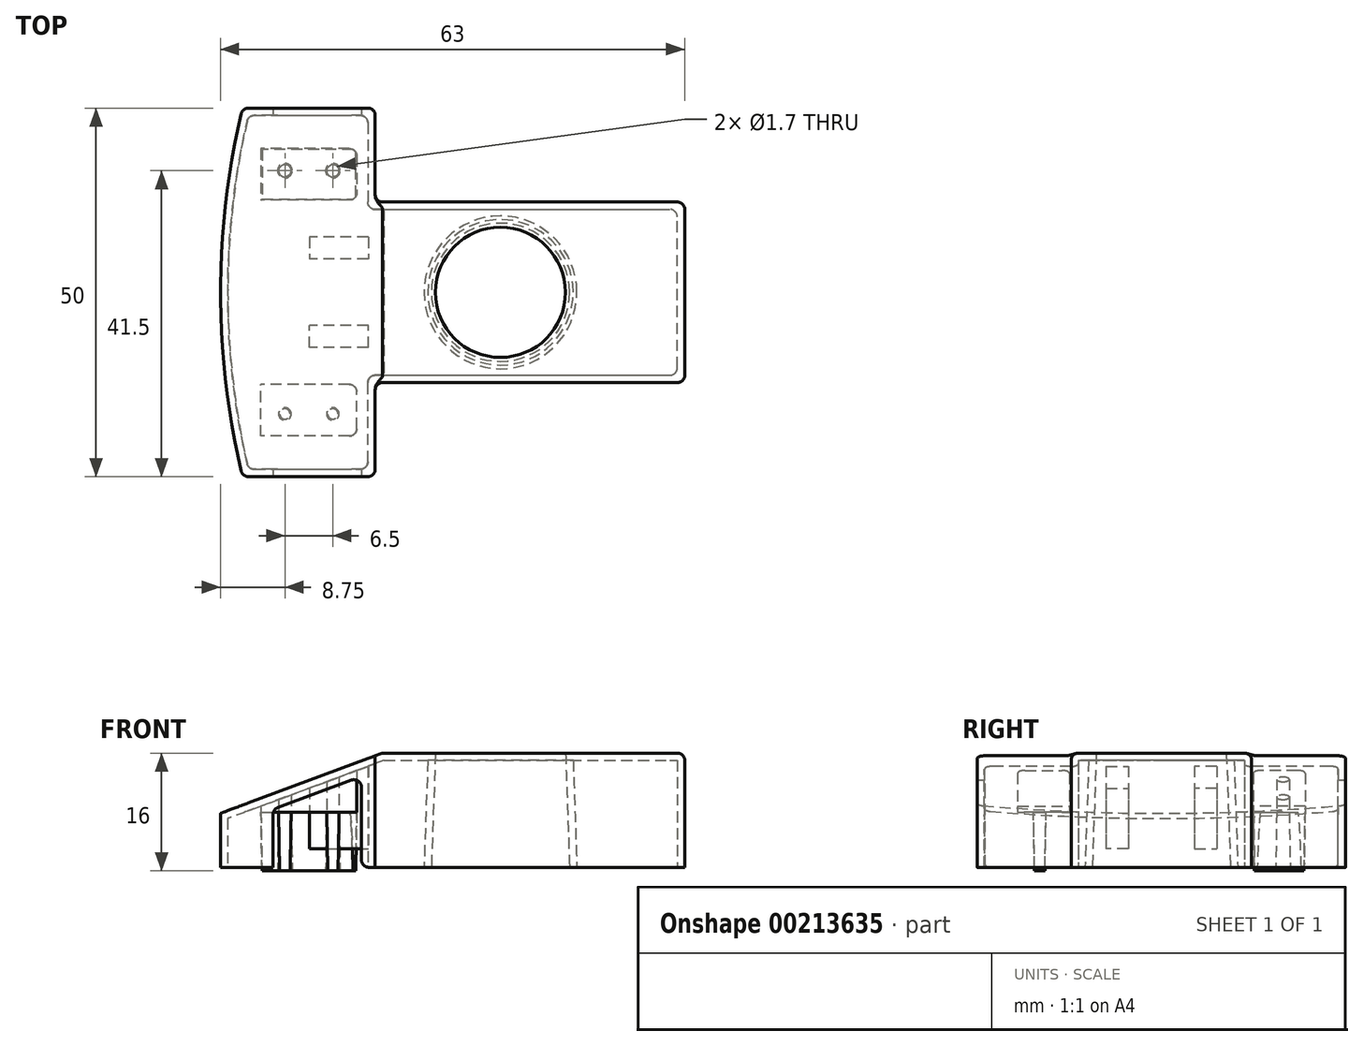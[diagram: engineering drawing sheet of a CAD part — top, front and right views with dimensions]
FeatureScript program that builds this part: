
annotation { "Feature Type Name" : "Feature", "Feature Type Description" : "" }
export const myFeature = defineFeature(function(context is Context, id is Id, definition is map)
    precondition{}
    {
        {
            var Q0;
            Q0=qCreatedBy(makeId("Top.planeOp"),FACE);
            var sketch = newSketch(context, id + "F0", { "sketchPlane" : qUnion([Q0])});
            skCircle(sketch, "E0", {"center": v(-4, 0) * mm, "radius": 9.37 * mm});
            skLineSegment(sketch, "E1.bottom", {"start": v(-21, -12.25) * mm, "end": v(21, -12.25) * mm});
            skLineSegment(sketch, "E1.top", {"start": v(-21, 12.25) * mm, "end": v(21, 12.25) * mm});
            skLineSegment(sketch, "E1.right", {"start": v(21, -12.25) * mm, "end": v(21, 12.25) * mm});
            skLineSegment(sketch, "E2.bottom", {"start": v(-21, -25) * mm, "end": v(-39, -25) * mm});
            skLineSegment(sketch, "E2.top", {"start": v(-21, 25) * mm, "end": v(-39, 25) * mm});
            skLineSegment(sketch, "E2.left", {"start": v(-21, -25) * mm, "end": v(-21, -12.25) * mm});
            skLineSegment(sketch, "E2.right", {"start": v(-39, -25) * mm, "end": v(-39, 25) * mm});
            skPoint(sketch, "E2.middle", {"position": v(-30, 0) * mm});
            skLineSegment(sketch, "E3.trimOffspring", {"start": v(-21, 12.25) * mm, "end": v(-21, 25) * mm});
            skLineSegment(sketch, "E4", {"start": v(-20, 12.25) * mm, "end": v(-20, -12.25) * mm});
            skPoint(sketch, "E5", {"position": v(-42, 0) * mm});
            skPoint(sketch, "E5.positionSnap0", {"position": v(-39, 0) * mm});
            skArc(sketch, "E6", {"start": v(-39, 25) * mm, "mid": v(-42, 0) * mm, "end": v(-39, -25) * mm});
            skSolve(sketch);
        }
        {
            var Q0;
            Q0=qSketchRegion(id+"F0",true);
            var Q1;
            Q1=makeQuery(id+"F0.imprint","IMPRINT",FACE,{"disambiguationData":[TD([[makeQuery(id+"F0.imprint","IMPRINT",EDGE,{"derivedFrom":sQuery(id+"F0.wireOp",EDGE,"E0")}),1.0]])]});
            extrude(context, id + "F1", {"entities" : qUnion([Q0, Q1]), "depth" : 15.5 * mm});
        }
        {
            var Q0;
            Q0=makeQuery(id+"F0.imprint","IMPRINT",FACE,{"disambiguationData":[TD([[makeQuery(id+"F0.imprint","IMPRINT",EDGE,{"derivedFrom":sQuery(id+"F0.wireOp",EDGE,"E0")}),1.0]])]});
            var Q1;
            Q1=makeQuery(id+"F1.opExtrude","CAP_FACE",FACE,{"disambiguationData":[OSD([sQuery(id+"F0.wireOp",EDGE,"E1.bottom"),sQuery(id+"F0.wireOp",EDGE,"E1.top"),sQuery(id+"F0.wireOp",EDGE,"E1.right"),sQuery(id+"F0.wireOp",EDGE,"E2.bottom"),sQuery(id+"F0.wireOp",EDGE,"E2.top"),sQuery(id+"F0.wireOp",EDGE,"E2.left"),sQuery(id+"F0.wireOp",EDGE,"E3.trimOffspring"),sQuery(id+"F0.wireOp",EDGE,"E6")])],"isStart":false});
            extrude(context, id + "F2", {"entities" : qUnion([Q0]), "operationType" : NewBodyOperationType.REMOVE, "endBound" : BoundingType.UP_TO_SURFACE, "endBoundEntityFace" : qUnion([Q1]), "depth" : 25 * mm, "hasDraft" : true, "draftAngle" : 2 * degree, "draftPullDirection" : true});
        }
        {
            var Q0;
            Q0=qCreatedBy(makeId("Front.planeOp"),FACE);
            var Q1;
            Q1=makeQuery(id+"F1.opExtrude","CAP_EDGE",EDGE,{"disambiguationData":[OSD([sQuery(id+"F0.wireOp",EDGE,"E2.bottom")])],"isStart":true});
            cPlane(context, id + "F3", {"entities" : qUnion([Q0, Q1]), "cplaneType" : CPlaneType.LINE_ANGLE, "offset" : 25 * mm, "angle" : 0 * degree, "width" : 150 * mm, "height" : 150 * mm});
        }
        {
            var Q0;
            Q0=qCreatedBy(id+"F3.planeOp",FACE);
            var sketch = newSketch(context, id + "F4", { "sketchPlane" : qUnion([Q0])});
            skLineSegment(sketch, "E7", {"start": v(20, 15.5) * mm, "end": v(42, 15.5) * mm});
            skLineSegment(sketch, "E8", {"start": v(42, 15.5) * mm, "end": v(42, 7.32) * mm});
            skLineSegment(sketch, "E9", {"start": v(42, 7.32) * mm, "end": v(20, 15.5) * mm});
            skLineSegment(sketch, "E10", {"start": v(42, 0) * mm, "end": v(41.46, 15.5) * mm, "construction": true});
            skLineSegment(sketch, "E11", {"start": v(42, 0) * mm, "end": v(42, 27.73) * mm, "construction": true});
            skSolve(sketch);
        }
        {
            var Q0;
            Q0=qSketchRegion(id+"F4",true);
            extrude(context, id + "F5", {"entities" : qUnion([Q0]), "operationType" : NewBodyOperationType.REMOVE, "endBound" : BoundingType.THROUGH_ALL, "depth" : 25 * mm});
        }
        {
            var Q0;
            Q0=makeQuery(id+"F1.opExtrude","CAP_FACE",FACE,{"disambiguationData":[OSD([sQuery(id+"F0.wireOp",EDGE,"E1.bottom"),sQuery(id+"F0.wireOp",EDGE,"E1.top"),sQuery(id+"F0.wireOp",EDGE,"E1.right"),sQuery(id+"F0.wireOp",EDGE,"E2.bottom"),sQuery(id+"F0.wireOp",EDGE,"E2.top"),sQuery(id+"F0.wireOp",EDGE,"E2.left"),sQuery(id+"F0.wireOp",EDGE,"E3.trimOffspring"),sQuery(id+"F0.wireOp",EDGE,"E6")])],"isStart":true});
            shell(context, id + "F6", {"entities" : qUnion([Q0]), "thickness" : 1 * mm});
        }
        {
            var Q0;
            Q0=makeQuery(id+"F1.opExtrude","SWEPT_FACE",FACE,{"disambiguationData":[OSD([sQuery(id+"F0.wireOp",EDGE,"E2.bottom")])]});
            var sketch = newSketch(context, id + "F7", { "sketchPlane" : qUnion([Q0])});
            skLineSegment(sketch, "E12", {"start": v(-20, 15.5) * mm, "end": v(-39, 8.43) * mm});
            skLineSegment(sketch, "E13", {"start": v(-39, 8.43) * mm, "end": v(-39, 15.5) * mm});
            skLineSegment(sketch, "E14", {"start": v(-39, 15.5) * mm, "end": v(-20, 15.5) * mm});
            skLineSegment(sketch, "E15", {"start": v(-34.87, 0) * mm, "end": v(-34.87, 7.86) * mm});
            skLineSegment(sketch, "E16", {"start": v(-34.87, 7.86) * mm, "end": v(-22.87, 12.32) * mm});
            skLineSegment(sketch, "E17", {"start": v(-22.87, 0) * mm, "end": v(-34.87, 0) * mm});
            skLineSegment(sketch, "E18", {"start": v(-22.87, 12.32) * mm, "end": v(-22.87, 0) * mm});
            skSolve(sketch);
        }
        {
            var Q0;
            Q0=makeQuery(id+"F7.imprint","IMPRINT",FACE,{"disambiguationData":[TD([[makeQuery(id+"F7.imprint","IMPRINT",EDGE,{"derivedFrom":sQuery(id+"F7.wireOp",EDGE,"E15")}),-1.0]])]});
            extrude(context, id + "F8", {"entities" : qUnion([Q0]), "operationType" : NewBodyOperationType.REMOVE, "endBound" : BoundingType.THROUGH_ALL, "oppositeDirection" : true, "depth" : 25 * mm});
        }
        {
            var Q0;
            Q0=makeQuery(id+"F1.opExtrude","CAP_FACE",FACE,{"disambiguationData":[OSD([sQuery(id+"F0.wireOp",EDGE,"E0"),sQuery(id+"F0.wireOp",EDGE,"E1.bottom"),sQuery(id+"F0.wireOp",EDGE,"E1.top"),sQuery(id+"F0.wireOp",EDGE,"E1.right"),sQuery(id+"F0.wireOp",EDGE,"E2.bottom"),sQuery(id+"F0.wireOp",EDGE,"E2.top"),sQuery(id+"F0.wireOp",EDGE,"E2.left"),sQuery(id+"F0.wireOp",EDGE,"E2.right"),sQuery(id+"F0.wireOp",EDGE,"E3.trimOffspring")])],"isStart":false});
            cPlane(context, id + "F9", {"entities" : qUnion([Q0]), "cplaneType" : CPlaneType.OFFSET, "offset" : 8 * mm, "oppositeDirection" : true, "width" : 150 * mm, "height" : 150 * mm});
        }
        {
            var Q0;
            Q0=qCreatedBy(id+"F9.planeOp",FACE);
            var sketch = newSketch(context, id + "F10", { "sketchPlane" : qUnion([Q0])});
            skLineSegment(sketch, "E19", {"start": v(0, 0) * mm, "end": v(-63, 0) * mm, "construction": true});
            skLineSegment(sketch, "E20.bottom", {"start": v(-36.5, -12.5) * mm, "end": v(-23.5, -12.5) * mm});
            skLineSegment(sketch, "E20.top", {"start": v(-36.5, -19.5) * mm, "end": v(-23.5, -19.5) * mm});
            skLineSegment(sketch, "E20.left", {"start": v(-36.5, -12.5) * mm, "end": v(-36.5, -19.5) * mm});
            skLineSegment(sketch, "E20.right", {"start": v(-23.5, -12.5) * mm, "end": v(-23.5, -19.5) * mm});
            skPoint(sketch, "E20.middle", {"position": v(-30, -16) * mm});
            skPoint(sketch, "E21", {"position": v(-33.25, -16.5) * mm});
            skPoint(sketch, "E22", {"position": v(-26.75, -16.5) * mm});
            skCircle(sketch, "E23", {"center": v(-33.25, -16.5) * mm, "radius": 0.85 * mm});
            skCircle(sketch, "E24", {"center": v(-26.75, -16.5) * mm, "radius": 0.85 * mm});
            skLineSegment(sketch, "E25.MirrorCS", {"start": v(-36.5, 12.5) * mm, "end": v(-23.5, 12.5) * mm});
            skLineSegment(sketch, "E26.MirrorCS", {"start": v(-36.5, 12.5) * mm, "end": v(-36.5, 19.5) * mm});
            skLineSegment(sketch, "E27.MirrorCS", {"start": v(-36.5, 19.5) * mm, "end": v(-23.5, 19.5) * mm});
            skLineSegment(sketch, "E28.MirrorCS", {"start": v(-23.5, 12.5) * mm, "end": v(-23.5, 19.5) * mm});
            skCircle(sketch, "E29.MirrorC", {"center": v(-26.75, 16.5) * mm, "radius": 0.85 * mm});
            skCircle(sketch, "E30.MirrorC", {"center": v(-33.25, 16.5) * mm, "radius": 0.85 * mm});
            skSolve(sketch);
        }
        {
            var Q0;
            Q0=makeQuery(id+"F10.imprint","IMPRINT",FACE,{"disambiguationData":[TD([[makeQuery(id+"F10.imprint","IMPRINT",EDGE,{"derivedFrom":sQuery(id+"F10.wireOp",EDGE,"E20.bottom")}),-1.0]])]});
            var Q1;
            Q1=makeQuery(id+"F10.imprint","IMPRINT",FACE,{"disambiguationData":[TD([[makeQuery(id+"F10.imprint","IMPRINT",EDGE,{"derivedFrom":sQuery(id+"F10.wireOp",EDGE,"E23")}),1.0]])]});
            var Q2;
            Q2=makeQuery(id+"F10.imprint","IMPRINT",FACE,{"disambiguationData":[TD([[makeQuery(id+"F10.imprint","IMPRINT",EDGE,{"derivedFrom":sQuery(id+"F10.wireOp",EDGE,"E24")}),1.0]])]});
            var Q3;
            Q3=makeQuery(id+"F10.imprint","IMPRINT",FACE,{"disambiguationData":[TD([[makeQuery(id+"F10.imprint","IMPRINT",EDGE,{"derivedFrom":sQuery(id+"F10.wireOp",EDGE,"E25.MirrorCS")}),1.0]])]});
            var Q4;
            Q4=makeQuery(id+"F10.imprint","IMPRINT",FACE,{"disambiguationData":[TD([[makeQuery(id+"F10.imprint","IMPRINT",EDGE,{"derivedFrom":sQuery(id+"F10.wireOp",EDGE,"E30.MirrorC")}),-1.0]])]});
            var Q5;
            Q5=makeQuery(id+"F10.imprint","IMPRINT",FACE,{"disambiguationData":[TD([[makeQuery(id+"F10.imprint","IMPRINT",EDGE,{"derivedFrom":sQuery(id+"F10.wireOp",EDGE,"E29.MirrorC")}),-1.0]])]});
            var Q6;
            Q6=makeQuery(id+"F6.opShell","OFFSET_FACE",FACE,{"disambiguationData":[OSD([sQuery(id+"F4.wireOp",EDGE,"E9")])]});
            extrude(context, id + "F11", {"entities" : qUnion([Q0, Q1, Q2, Q3, Q4, Q5]), "operationType" : NewBodyOperationType.ADD, "endBound" : BoundingType.UP_TO_SURFACE, "endBoundEntityFace" : qUnion([Q6]), "depth" : 25 * mm});
        }
        {
            var Q0;
            Q0=makeQuery(id+"F10.imprint","IMPRINT",FACE,{"disambiguationData":[TD([[makeQuery(id+"F10.imprint","IMPRINT",EDGE,{"derivedFrom":sQuery(id+"F10.wireOp",EDGE,"E23")}),1.0]])]});
            var Q1;
            Q1=makeQuery(id+"F10.imprint","IMPRINT",FACE,{"disambiguationData":[TD([[makeQuery(id+"F10.imprint","IMPRINT",EDGE,{"derivedFrom":sQuery(id+"F10.wireOp",EDGE,"E29.MirrorC")}),-1.0]])]});
            var Q2;
            Q2=makeQuery(id+"F10.imprint","IMPRINT",FACE,{"disambiguationData":[TD([[makeQuery(id+"F10.imprint","IMPRINT",EDGE,{"derivedFrom":sQuery(id+"F10.wireOp",EDGE,"E30.MirrorC")}),-1.0]])]});
            var Q3;
            Q3=makeQuery(id+"F10.imprint","IMPRINT",FACE,{"disambiguationData":[TD([[makeQuery(id+"F10.imprint","IMPRINT",EDGE,{"derivedFrom":sQuery(id+"F10.wireOp",EDGE,"E24")}),1.0]])]});
            extrude(context, id + "F12", {"entities" : qUnion([Q0, Q1, Q2, Q3]), "operationType" : NewBodyOperationType.ADD, "oppositeDirection" : true, "depth" : 8 * mm, "hasDraft" : true, "draftAngle" : 1 * degree, "draftPullDirection" : true});
        }
        {
            var Q0;
            Q0=makeQuery(id+"F1.opExtrude","CAP_EDGE",EDGE,{"disambiguationData":[OSD([sQuery(id+"F0.wireOp",EDGE,"E1.bottom")])],"isStart":false});
            var Q1;
            Q1=makeQuery(id+"F1.opExtrude","CAP_EDGE",EDGE,{"disambiguationData":[OSD([sQuery(id+"F0.wireOp",EDGE,"E1.right")])],"isStart":false});
            var Q2;
            Q2=makeQuery(id+"F1.opExtrude","CAP_EDGE",EDGE,{"disambiguationData":[OSD([sQuery(id+"F0.wireOp",EDGE,"E1.top")])],"isStart":false});
            var Q3;
            Q3=makeQuery(id+"F1.opExtrude","SWEPT_EDGE",EDGE,{"disambiguationData":[OSD([sQuery(id+"F0.wireOp",EDGE,"E1.bottom"),sQuery(id+"F0.wireOp",EDGE,"E1.right")])]});
            var Q4;
            Q4=makeQuery(id+"F1.opExtrude","SWEPT_EDGE",EDGE,{"disambiguationData":[OSD([sQuery(id+"F0.wireOp",EDGE,"E1.top"),sQuery(id+"F0.wireOp",EDGE,"E1.right")])]});
            fillet(context, id + "F13", {"entities" : qUnion([Q0, Q1, Q2, Q3, Q4]), "radius" : 1 * mm, "tangentPropagation" : true, "allowEdgeOverflow" : false});
        }
        {
            var Q0;
            Q0=makeQuery(id+"F1.opExtrude","SWEPT_EDGE",EDGE,{"disambiguationData":[OSD([sQuery(id+"F0.wireOp",EDGE,"E2.bottom"),sQuery(id+"F0.wireOp",EDGE,"E2.left")])]});
            var Q1;
            Q1=makeQuery(id+"F5.boolean.opBoolean","INTERSECT",EDGE,{"derivedFrom":[makeQuery(id+"F1.opExtrude","SWEPT_FACE",FACE,{"disambiguationData":[OSD([sQuery(id+"F0.wireOp",EDGE,"E2.left")])]}),makeQuery(id+"F5.opExtrude","SWEPT_FACE",FACE,{"disambiguationData":[OSD([sQuery(id+"FjstzwEYRuGCUyq_1.wireOp",EDGE,"6156deb2-2619-4c56-9df6-34b3699534c4")])]})]});
            var Q2;
            Q2=makeQuery(id+"F5.boolean.opBoolean","COPY",EDGE,{"derivedFrom":makeQuery(id+"F5.opExtrude","CAP_EDGE",EDGE,{"disambiguationData":[OSD([sQuery(id+"FjstzwEYRuGCUyq_1.wireOp",EDGE,"6156deb2-2619-4c56-9df6-34b3699534c4")])],"isStart":true})});
            var Q3;
            Q3=makeQuery(id+"F1.opExtrude","SWEPT_EDGE",EDGE,{"disambiguationData":[OSD([sQuery(id+"F0.wireOp",EDGE,"E2.bottom"),sQuery(id+"F0.wireOp",EDGE,"E2.right"),sQuery(id+"F0.wireOp",EDGE,"E6")])]});
            var Q4;
            Q4=makeQuery(id+"F5.boolean.opBoolean","INTERSECT",EDGE,{"derivedFrom":[makeQuery(id+"F1.opExtrude","SWEPT_FACE",FACE,{"disambiguationData":[OSD([sQuery(id+"F0.wireOp",EDGE,"E6")])]}),makeQuery(id+"F5.opExtrude","SWEPT_FACE",FACE,{"disambiguationData":[OSD([sQuery(id+"FjstzwEYRuGCUyq_1.wireOp",EDGE,"6156deb2-2619-4c56-9df6-34b3699534c4")])]})]});
            var Q5;
            Q5=makeQuery(id+"F5.boolean.opBoolean","INTERSECT",EDGE,{"derivedFrom":[makeQuery(id+"F1.opExtrude","SWEPT_FACE",FACE,{"disambiguationData":[OSD([sQuery(id+"F0.wireOp",EDGE,"E2.top")])]}),makeQuery(id+"F5.opExtrude","SWEPT_FACE",FACE,{"disambiguationData":[OSD([sQuery(id+"FjstzwEYRuGCUyq_1.wireOp",EDGE,"6156deb2-2619-4c56-9df6-34b3699534c4")])]})]});
            var Q6;
            Q6=makeQuery(id+"F1.opExtrude","SWEPT_EDGE",EDGE,{"disambiguationData":[OSD([sQuery(id+"F0.wireOp",EDGE,"E2.top"),sQuery(id+"F0.wireOp",EDGE,"E2.right"),sQuery(id+"F0.wireOp",EDGE,"E6")])]});
            var Q7;
            Q7=makeQuery(id+"F1.opExtrude","SWEPT_EDGE",EDGE,{"disambiguationData":[OSD([sQuery(id+"F0.wireOp",EDGE,"E2.top"),sQuery(id+"F0.wireOp",EDGE,"E3.trimOffspring")])]});
            var Q8;
            Q8=makeQuery(id+"F5.boolean.opBoolean","INTERSECT",EDGE,{"derivedFrom":[makeQuery(id+"F1.opExtrude","SWEPT_FACE",FACE,{"disambiguationData":[OSD([sQuery(id+"F0.wireOp",EDGE,"E3.trimOffspring")])]}),makeQuery(id+"F5.opExtrude","SWEPT_FACE",FACE,{"disambiguationData":[OSD([sQuery(id+"FjstzwEYRuGCUyq_1.wireOp",EDGE,"6156deb2-2619-4c56-9df6-34b3699534c4")])]})]});
            fillet(context, id + "F14", {"entities" : qUnion([Q0, Q1, Q2, Q3, Q4, Q5, Q6, Q7, Q8]), "radius" : 1 * mm, "tangentPropagation" : true, "allowEdgeOverflow" : false});
        }
        {
            var Q0;
            Q0=makeQuery(id+"F1.opExtrude","SWEPT_EDGE",EDGE,{"disambiguationData":[OSD([sQuery(id+"F0.wireOp",EDGE,"E1.top"),sQuery(id+"F0.wireOp",EDGE,"E3.trimOffspring")])]});
            fillet(context, id + "F15", {"entities" : qUnion([Q0]), "radius" : 1 * mm, "tangentPropagation" : true, "allowEdgeOverflow" : false});
        }
        {
            var Q0;
            Q0=makeQuery(id+"F1.opExtrude","SWEPT_EDGE",EDGE,{"disambiguationData":[OSD([sQuery(id+"F0.wireOp",EDGE,"E1.bottom"),sQuery(id+"F0.wireOp",EDGE,"E2.left")])]});
            var Q1;
            {var subQ0=sQuery(id+"F0.wireOp",EDGE,"E2.bottom");var subQ1=sQuery(id+"F7.wireOp",EDGE,"E18");Q1=makeQuery(id+"F8.boolean.opBoolean","COPY",EDGE,{"disambiguationData":[TD([makeQuery(id+"F1.opExtrude","SWEPT_FACE",FACE,{"disambiguationData":[OSD([subQ0])]})])],"derivedFrom":makeQuery(id+"F8.opExtrude","SWEPT_EDGE",EDGE,{"disambiguationData":[OSD([subQ0,sQuery(id+"F7.wireOp",EDGE,"E17"),subQ1])]})});}
            var Q2;
            {var subQ0=sQuery(id+"F0.wireOp",EDGE,"E2.bottom");var subQ1=sQuery(id+"F7.wireOp",EDGE,"E15");Q2=makeQuery(id+"F8.boolean.opBoolean","COPY",EDGE,{"disambiguationData":[TD([makeQuery(id+"F1.opExtrude","SWEPT_FACE",FACE,{"disambiguationData":[OSD([subQ0])]})])],"derivedFrom":makeQuery(id+"F8.opExtrude","SWEPT_EDGE",EDGE,{"disambiguationData":[OSD([subQ0,subQ1,sQuery(id+"F7.wireOp",EDGE,"E17")])]})});}
            var Q3;
            {var subQ0=sQuery(id+"F0.wireOp",EDGE,"E2.top");var subQ1=sQuery(id+"F0.wireOp",EDGE,"E2.bottom");var subQ2=sQuery(id+"F7.wireOp",EDGE,"E15");Q3=makeQuery(id+"F8.boolean.opBoolean","COPY",EDGE,{"disambiguationData":[TD([makeQuery(id+"F1.opExtrude","SWEPT_FACE",FACE,{"disambiguationData":[OSD([subQ0])]})])],"derivedFrom":makeQuery(id+"F8.opExtrude","SWEPT_EDGE",EDGE,{"disambiguationData":[OSD([subQ1,subQ2,sQuery(id+"F7.wireOp",EDGE,"E17")])]})});}
            var Q4;
            {var subQ0=sQuery(id+"F0.wireOp",EDGE,"E2.top");var subQ1=sQuery(id+"F0.wireOp",EDGE,"E2.bottom");var subQ2=sQuery(id+"F7.wireOp",EDGE,"E18");Q4=makeQuery(id+"F8.boolean.opBoolean","COPY",EDGE,{"disambiguationData":[TD([makeQuery(id+"F1.opExtrude","SWEPT_FACE",FACE,{"disambiguationData":[OSD([subQ0])]})])],"derivedFrom":makeQuery(id+"F8.opExtrude","SWEPT_EDGE",EDGE,{"disambiguationData":[OSD([subQ1,sQuery(id+"F7.wireOp",EDGE,"E17"),subQ2])]})});}
            var Q5;
            {var subQ0=sQuery(id+"F0.wireOp",EDGE,"E2.top");var subQ1=sQuery(id+"F7.wireOp",EDGE,"E18");var subQ2=sQuery(id+"F7.wireOp",EDGE,"E16");Q5=makeQuery(id+"F8.boolean.opBoolean","COPY",EDGE,{"disambiguationData":[TD([makeQuery(id+"F1.opExtrude","SWEPT_FACE",FACE,{"disambiguationData":[OSD([subQ0])]})])],"derivedFrom":makeQuery(id+"F8.opExtrude","SWEPT_EDGE",EDGE,{"disambiguationData":[OSD([subQ2,subQ1])]})});}
            var Q6;
            {var subQ0=sQuery(id+"F0.wireOp",EDGE,"E2.top");var subQ1=sQuery(id+"F7.wireOp",EDGE,"E15");var subQ2=sQuery(id+"F7.wireOp",EDGE,"E16");Q6=makeQuery(id+"F8.boolean.opBoolean","COPY",EDGE,{"disambiguationData":[TD([makeQuery(id+"F1.opExtrude","SWEPT_FACE",FACE,{"disambiguationData":[OSD([subQ0])]})])],"derivedFrom":makeQuery(id+"F8.opExtrude","SWEPT_EDGE",EDGE,{"disambiguationData":[OSD([subQ1,subQ2])]})});}
            var Q7;
            {var subQ0=sQuery(id+"F0.wireOp",EDGE,"E2.bottom");var subQ1=sQuery(id+"F7.wireOp",EDGE,"E18");var subQ2=sQuery(id+"F7.wireOp",EDGE,"E16");Q7=makeQuery(id+"F8.boolean.opBoolean","COPY",EDGE,{"disambiguationData":[TD([makeQuery(id+"F1.opExtrude","SWEPT_FACE",FACE,{"disambiguationData":[OSD([subQ0])]})])],"derivedFrom":makeQuery(id+"F8.opExtrude","SWEPT_EDGE",EDGE,{"disambiguationData":[OSD([subQ2,subQ1])]})});}
            var Q8;
            {var subQ0=sQuery(id+"F0.wireOp",EDGE,"E2.bottom");var subQ1=sQuery(id+"F7.wireOp",EDGE,"E15");var subQ2=sQuery(id+"F7.wireOp",EDGE,"E16");Q8=makeQuery(id+"F8.boolean.opBoolean","COPY",EDGE,{"disambiguationData":[TD([makeQuery(id+"F1.opExtrude","SWEPT_FACE",FACE,{"disambiguationData":[OSD([subQ0])]})])],"derivedFrom":makeQuery(id+"F8.opExtrude","SWEPT_EDGE",EDGE,{"disambiguationData":[OSD([subQ1,subQ2])]})});}
            var Q9;
            Q9=makeQuery(id+"F6.opShell","OFFSET_EDGE",EDGE,{"disambiguationData":[OSD([sQuery(id+"F0.wireOp",EDGE,"E1.top"),sQuery(id+"F0.wireOp",EDGE,"E3.trimOffspring")])]});
            var Q10;
            Q10=makeQuery(id+"F6.opShell","OFFSET_EDGE",EDGE,{"disambiguationData":[OSD([sQuery(id+"F0.wireOp",EDGE,"E1.bottom"),sQuery(id+"F0.wireOp",EDGE,"E2.left")])]});
            fillet(context, id + "F16", {"entities" : qUnion([Q0, Q1, Q2, Q3, Q4, Q5, Q6, Q7, Q8, Q9, Q10]), "radius" : 1 * mm, "tangentPropagation" : true, "allowEdgeOverflow" : false});
        }
        {
            var Q0;
            Q0=makeQuery(id+"F6.opShell","OFFSET_EDGE",EDGE,{"disambiguationData":[OSD([sQuery(id+"F0.wireOp",EDGE,"E1.top"),sQuery(id+"F0.wireOp",EDGE,"E1.right")])]});
            var Q1;
            Q1=makeQuery(id+"F6.opShell","OFFSET_EDGE",EDGE,{"disambiguationData":[OSD([sQuery(id+"F0.wireOp",EDGE,"E1.bottom"),sQuery(id+"F0.wireOp",EDGE,"E1.right")])]});
            var Q2;
            {var subQ0=sQuery(id+"F0.wireOp",EDGE,"E0");Q2=makeQuery(id+"F6.opShell","OFFSET_EDGE",EDGE,{"disambiguationData":[OSD([subQ0]),TDD([makeQuery(id+"F1.opExtrude","CAP_EDGE",EDGE,{"disambiguationData":[OSD([subQ0])],"isStart":false})])]});}
            var Q3;
            Q3=makeQuery(id+"F6.opShell","OFFSET_EDGE",EDGE,{"disambiguationData":[OSD([sQuery(id+"F0.wireOp",EDGE,"E2.top"),sQuery(id+"F0.wireOp",EDGE,"E3.trimOffspring")])]});
            var Q4;
            Q4=makeQuery(id+"F6.opShell","OFFSET_EDGE",EDGE,{"disambiguationData":[OSD([sQuery(id+"F0.wireOp",EDGE,"E2.top"),sQuery(id+"F0.wireOp",EDGE,"E2.right"),sQuery(id+"F0.wireOp",EDGE,"E6")])]});
            var Q5;
            Q5=makeQuery(id+"F6.opShell","OFFSET_EDGE",EDGE,{"disambiguationData":[OSD([sQuery(id+"F0.wireOp",EDGE,"E2.bottom"),sQuery(id+"F0.wireOp",EDGE,"E2.left")])]});
            var Q6;
            Q6=makeQuery(id+"F6.opShell","OFFSET_EDGE",EDGE,{"disambiguationData":[OSD([sQuery(id+"F0.wireOp",EDGE,"E2.bottom"),sQuery(id+"F0.wireOp",EDGE,"E2.right"),sQuery(id+"F0.wireOp",EDGE,"E6")])]});
            var Q7;
            Q7=makeQuery(id+"F11.opExtrude","SWEPT_EDGE",EDGE,{"disambiguationData":[OSD([sQuery(id+"F10.wireOp",EDGE,"E20.bottom"),sQuery(id+"F10.wireOp",EDGE,"E20.right")])]});
            var Q8;
            Q8=makeQuery(id+"F11.opExtrude","SWEPT_EDGE",EDGE,{"disambiguationData":[OSD([sQuery(id+"F10.wireOp",EDGE,"E20.top"),sQuery(id+"F10.wireOp",EDGE,"E20.right")])]});
            var Q9;
            Q9=makeQuery(id+"F11.opExtrude","SWEPT_EDGE",EDGE,{"disambiguationData":[OSD([sQuery(id+"F10.wireOp",EDGE,"E27.MirrorCS"),sQuery(id+"F10.wireOp",EDGE,"E28.MirrorCS")])]});
            var Q10;
            Q10=makeQuery(id+"F11.opExtrude","SWEPT_EDGE",EDGE,{"disambiguationData":[OSD([sQuery(id+"F10.wireOp",EDGE,"E25.MirrorCS"),sQuery(id+"F10.wireOp",EDGE,"E28.MirrorCS")])]});
            fillet(context, id + "F17", {"entities" : qUnion([Q0, Q1, Q2, Q3, Q4, Q5, Q6, Q7, Q8, Q9, Q10]), "radius" : 1 * mm, "tangentPropagation" : true, "allowEdgeOverflow" : false});
        }
        {
            var Q0;
            Q0=qCreatedBy(id+"F9.planeOp",FACE);
            var sketch = newSketch(context, id + "F18", { "sketchPlane" : qUnion([Q0])});
            skPoint(sketch, "E31", {"position": v(-29.94, -4.5) * mm});
            skLineSegment(sketch, "E32.bottom", {"start": v(-29.94, -4.5) * mm, "end": v(-21.94, -4.5) * mm});
            skLineSegment(sketch, "E32.top", {"start": v(-29.94, -7.5) * mm, "end": v(-21.94, -7.5) * mm});
            skLineSegment(sketch, "E32.left", {"start": v(-29.94, -4.5) * mm, "end": v(-29.94, -7.5) * mm});
            skLineSegment(sketch, "E32.right", {"start": v(-21.94, -4.5) * mm, "end": v(-21.94, -7.5) * mm});
            skLineSegment(sketch, "E33", {"start": v(0, 0) * mm, "end": v(-48.4, 0) * mm, "construction": true});
            skLineSegment(sketch, "E34.MirrorCS", {"start": v(-29.94, 4.5) * mm, "end": v(-21.94, 4.5) * mm});
            skLineSegment(sketch, "E35.MirrorCS", {"start": v(-21.94, 4.5) * mm, "end": v(-21.94, 7.5) * mm});
            skLineSegment(sketch, "E36.MirrorCS", {"start": v(-29.94, 7.5) * mm, "end": v(-21.94, 7.5) * mm});
            skLineSegment(sketch, "E37.MirrorCS", {"start": v(-29.94, 4.5) * mm, "end": v(-29.94, 7.5) * mm});
            skSolve(sketch);
        }
        {
            var Q0;
            Q0=qSketchRegion(id+"F18",true);
            var Q1;
            Q1=makeQuery(id+"F6.opShell","OFFSET_FACE",FACE,{"disambiguationData":[OSD([sQuery(id+"F4.wireOp",EDGE,"E9")])]});
            extrude(context, id + "F19", {"entities" : qUnion([Q0]), "operationType" : NewBodyOperationType.ADD, "endBound" : BoundingType.UP_TO_SURFACE, "endBoundEntityFace" : qUnion([Q1]), "depth" : 25 * mm, "hasSecondDirection" : true, "secondDirectionOppositeDirection" : true, "secondDirectionDepth" : 5 * mm});
        }
    });
